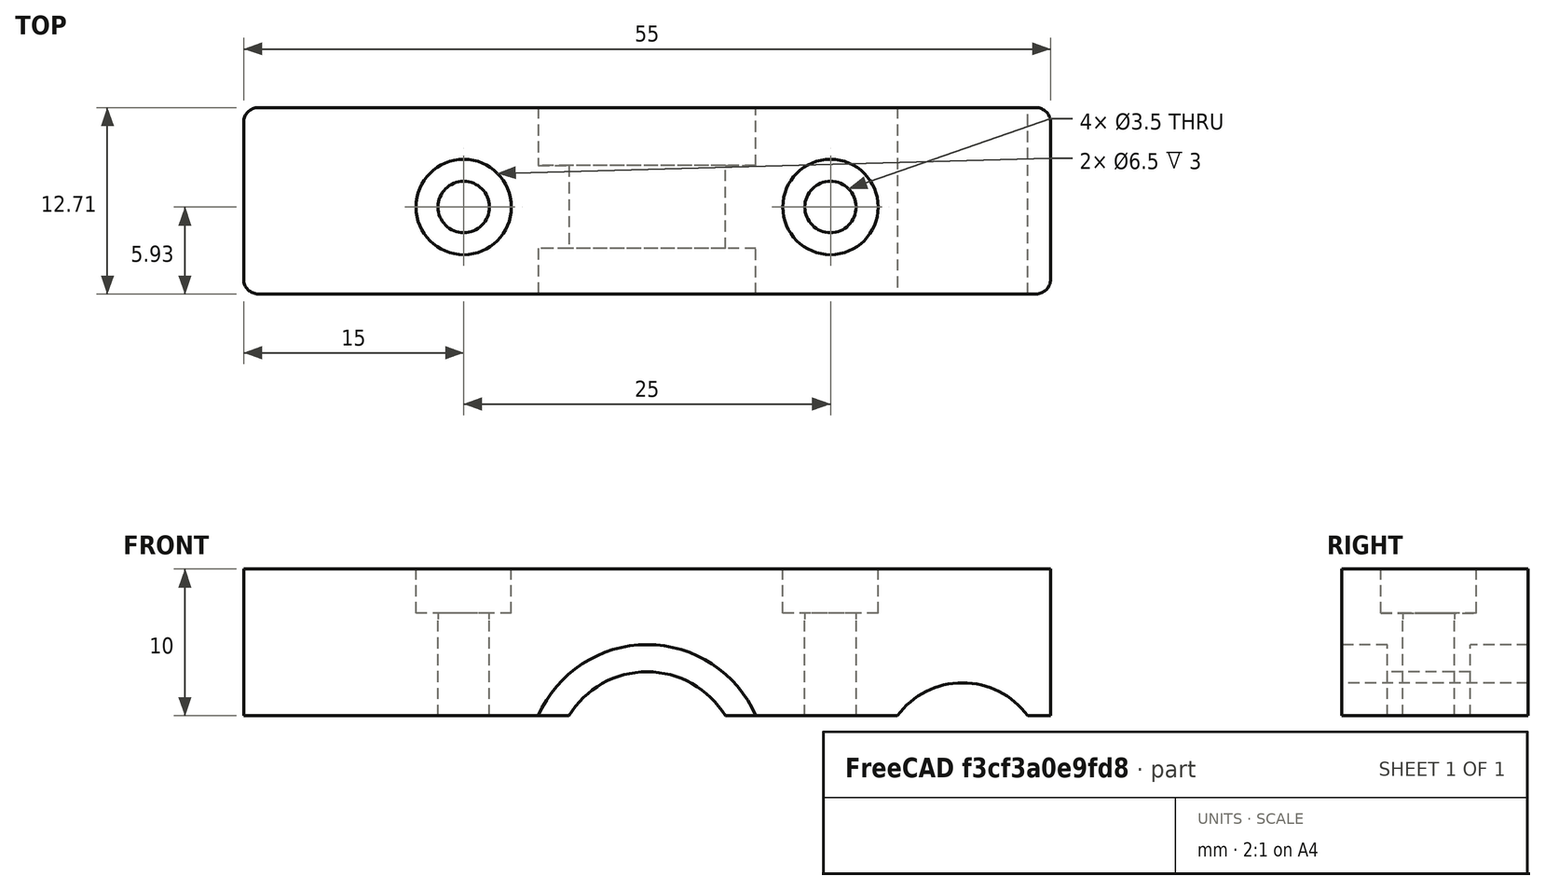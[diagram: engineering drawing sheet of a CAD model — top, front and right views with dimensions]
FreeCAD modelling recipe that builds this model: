
FCSTD DOCUMENT  (FreeCAD 0.17R13424 (Git))
Label: HCevo_Hotend_Retainer_1_0
License: All rights reserved
LicenseURL: http://en.wikipedia.org/wiki/All_rights_reserved
objects: PartDesign::Pocket×2, Part::Feature×1, PartDesign::FeatureBase×1, PartDesign::Body×1
note: 7 computed .brp shape members not serialized (recipe doc carries the construction recipe); baked Part::Feature solids carry a one-line shape summary decoded from their .brp

FEATURE [Part::Feature] Part__Feature  label="Retainer"
  shape: bbox 55 x 12.7 x 10 mm, 26 faces (baked)
FEATURE [PartDesign::FeatureBase] BaseFeature
  BaseFeature = -> Part__Feature
FEATURE [PartDesign::Pocket] Pocket
  BaseFeature = -> BaseFeature
  Length = 5
  Length2 = 100
  Profile = -> BaseFeature [Face10]
  Type = 1
FEATURE [PartDesign::Pocket] Pocket001
  BaseFeature = -> Pocket
  Length = 5
  Length2 = 100
  Profile = -> Pocket [Face26]
  Type = 1
FEATURE [PartDesign::Body] Body
  BaseFeature = -> Part__Feature
  Group = -> [BaseFeature,Pocket,Pocket001]
  Origin = -> Origin
  Tip = -> Pocket001
